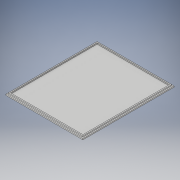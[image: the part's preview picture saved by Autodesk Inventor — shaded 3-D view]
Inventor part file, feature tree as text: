
AUTODESK INVENTOR PART (.ipt)
format: ipt  version: 2019 (Build 230136000, 136)  size: 121,344 bytes
history: native  units: in
note: dims shown in document units (in); Inventor stores cm internally (conversion verified against a paired STEP export)
features: extrude x3, sketch x3
ambient origin geometry x8: Origin, YZ Plane, XZ Plane, XY Plane, X Axis, Y Axis, Z Axis, Center Point
bodies: Solid1 (feature_tree)
feature tree (6):
  extrude  "Extrusion1"  Depth=8.0in
  extrude  "Extrusion3"  Depth=0.2in TaperAngle=0.0deg
  extrude  "Extrusion4"  Depth=0.1in
  sketch  "Sketch1"  dims[d0=6.75in d2=8.0in]
  sketch  "Sketch4"  dims[d3=0.1in d4=0.0in d18=0.2in d19=0.0in]
  sketch  "Sketch6"  dims[d20=0.1in d21=0.1in d22=0.1in d23=0.1in d24=0.1in d25=0.1in d26=0.1in d27=0.1in d28=0.1in d29=0.0in]
